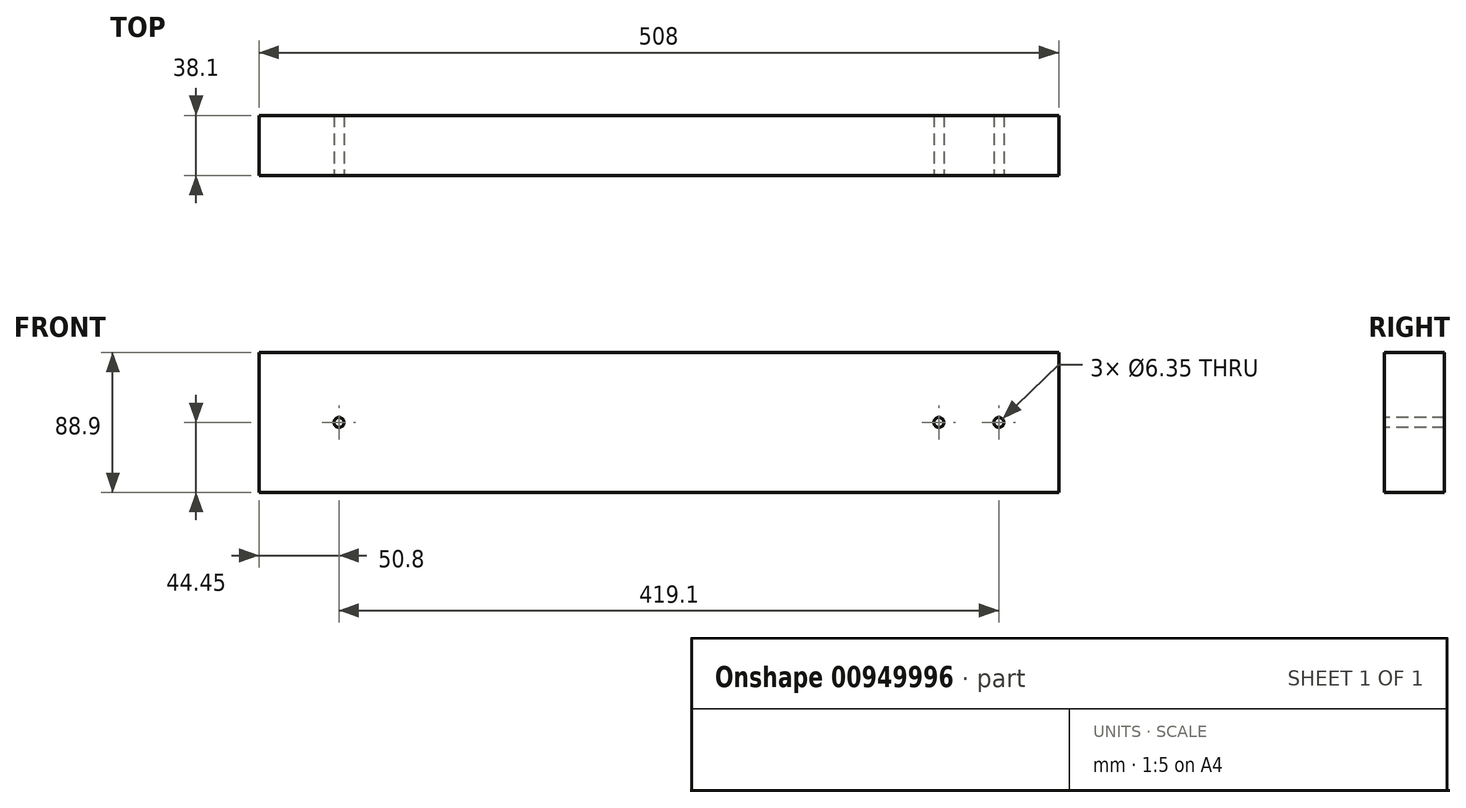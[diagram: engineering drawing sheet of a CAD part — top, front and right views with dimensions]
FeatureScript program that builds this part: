
annotation { "Feature Type Name" : "Feature", "Feature Type Description" : "" }
export const myFeature = defineFeature(function(context is Context, id is Id, definition is map)
    precondition{}
    {
        {
            var Q0;
            Q0=qCreatedBy(makeId("Right.planeOp"),FACE);
            var sketch = newSketch(context, id + "F0", { "sketchPlane" : qUnion([Q0])});
            skLineSegment(sketch, "E0.bottom", {"start": v(0, 88.9) * mm, "end": v(-38.1, 88.9) * mm});
            skLineSegment(sketch, "E0.top", {"start": v(0, 0) * mm, "end": v(-38.1, 0) * mm});
            skLineSegment(sketch, "E0.left", {"start": v(0, 88.9) * mm, "end": v(0, 0) * mm});
            skLineSegment(sketch, "E0.right", {"start": v(-38.1, 88.9) * mm, "end": v(-38.1, 0) * mm});
            skSolve(sketch);
        }
        {
            var Q0;
            Q0 = qSketchRegion(id + "F0", true);
            extrude(context, id + "F1", {"entities" : qUnion([Q0]), "endBound" : BoundingType.SYMMETRIC, "depth" : 508 * mm, "offsetDistance" : 25.4 * mm});
        }
        {
            var Q0;
            Q0=makeQuery(id+"F1.opExtrude","SWEPT_FACE",FACE,{"disambiguationData":[OSD([sQuery(id+"F0.wireOp",EDGE,"E0.right")])]});
            var sketch = newSketch(context, id + "F2", { "sketchPlane" : qUnion([Q0])});
            skPoint(sketch, "E1", {"position": v(-203.2, 44.45) * mm});
            skPoint(sketch, "E2", {"position": v(177.8, 44.45) * mm});
            skLineSegment(sketch, "E3", {"start": v(-203.2, 44.45) * mm, "end": v(254, 44.45) * mm, "construction": true});
            skPoint(sketch, "E4", {"position": v(215.9, 44.45) * mm});
            skSolve(sketch);
        }
        {
            var Q0;
            Q0=sQuery(id+"F2.wireOp",VERTEX,"E4");
            var Q1;
            Q1=sQuery(id+"F2.wireOp",VERTEX,"E2");
            var Q2;
            Q2=sQuery(id+"F2.wireOp",VERTEX,"E1");
            var Q3;
            Q3=makeQuery(id+"F1.opExtrude","SWEPT_BODY",BODY,{"disambiguationData":[OSD([sQuery(id+"F0.wireOp",EDGE,"E0.bottom"),sQuery(id+"F0.wireOp",EDGE,"E0.top"),sQuery(id+"F0.wireOp",EDGE,"E0.left"),sQuery(id+"F0.wireOp",EDGE,"E0.right")])]});
            hole(context, id + "F3", {"style" : HoleStyle.SIMPLE, "endStyle" : HoleEndStyle.THROUGH, "holeDiameter" : 6.35 * mm, "majorDiameter" : 6.35 * mm, "isTappedThrough" : true, "tappedDepth" : 12.7 * mm, "tapClearance" : 3, "startFromSketch" : true, "locations" : qUnion([Q0, Q1, Q2]), "scope" : qUnion([Q3])});
        }
    });
